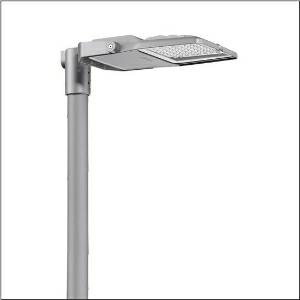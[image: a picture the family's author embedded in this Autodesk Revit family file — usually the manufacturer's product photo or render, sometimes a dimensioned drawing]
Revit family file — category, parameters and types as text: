
# Revit family: floodlight_fl_21_iq_mini___pl52_5xa7771c2d3a_33da
name_source: partatom
category: Lighting Fixtures
units: mm (PartAtom-declared; Revit-internal decimal feet)

## family parameters
Cut with Voids When Loaded = No
Host = Face
Light Source = No
Part Type = Normal
Room Calculation Point = No
Round Connector Dimension = Use Diameter
Shared = No

## types (1)
- --- (1 x LED, 12210 lm, 87.2 W, 3000K)
    Apparent Load = 87 VA
    CIE Flux Codes = 26 60 98 100 100
    Color Rendering = 70
    Color Temperature = 3000K
    Default Elevation = 1800 mm
    Description = Floodlight FL 21 iQ mini, floodlight, primary light control with lens, of PMMA, primary optical cover: protective disc, of toughened safety glass, transparent, light distribution: PL52, light emission: direct distribution, installation type: surface-mounted, LED, High Power LED, rated luminous flux: 12.210lm, luminous efficacy: 140lm/W, light colour: 730, colour temperature: 3000K, control gear: iQ Comfort/DALI, control: Auto-Match, Temp-Guard, Lumen-Switch, Night-Set, Smart-Wire, Light-Fading, Desk-Remote (wireless, voltage-free reading and setting of iQ features in the workshop via application-optimized NFC function/RFID function), optimised constant luminous flux control (CLO 2.0), with terminal, 6-pole, mains connection: 220..240V, AC, 50/60Hz, start of lifetime: 87W, end of service life: 92W, reduction: 40W, luminaire housing, of diecast aluminium, powder-coated, Siteco® metallic grey (DB 702S), corrosivity category C5 mid according to DIN EN ISO 12944, suitable for swimming pools, chlorine-resistant, sealing non-destructively replaceable, please order mast flange separately, mast bracket, of steel, galvanised, powder-coated, Siteco® metallic grey (DB 702S), protection rating (complete): IP66, insulation class (complete): insulation class II (safety insulation), certification: CE, ENEC, VDE, protection symbol: D, impact resistance: IK08, permissible operating ambient temperature: -40..+40°C, permissible operating ambient temperature for outdoor applications: -40..+50°C, standard: DIN EN 12944, LABS conformity tested according to VDMA 24364:2018-05, packaging unit: 1 piece

Light Distribution: PL52
    Height = 70 mm
    Lamp = 1 x LED
    Lamp Light Flux = 12210 lm
    Lamp Power = 87.2 W
    Lamp count = 1
    Length = 485 mm
    Luminous efficacy = 140 lm/W
    Manufacturer = Siteco
    ModVariant = No
    Model = 5XA7771C2D3A
    Number of Poles = 1
    OnlyDefault = Yes
    Power Factor = 1
    Product Name = Floodlight FL 21 iQ mini | PL52
    Product group = floodlight | pylon annexe
    ProductGroupID = 6201
    Protection Class = Protection class II
    Protection Degree = IP 66
    RLX_Detail_Level = 1
    RLX_Emergency_Light_Flux = 0 lm
    RLX_Emergency_Type = 0
    RLX_Emergency_Type_DB = No
    RlxData = <blob elided: 101545 chars, md5=4738f2f8>
    Socket = socket
    Standby Power = 0 W
    System Light Flux = 12210 lm
    System Power = 87 W
    Type Comments = factory setting: luminous flux: 100 % | dim-lin: 254 | 456 mA
    Type Image = l_1007125.jpg
    URL = http://relux.com
    VarID = @adj_186013
    Voltage = 0 V
    Weight = 0.00 kg
    Width = 337 mm

## geometry (parser evidence)
native form markers: Blend x4, Sweep x11
no freeform markers — native parametric forms only
